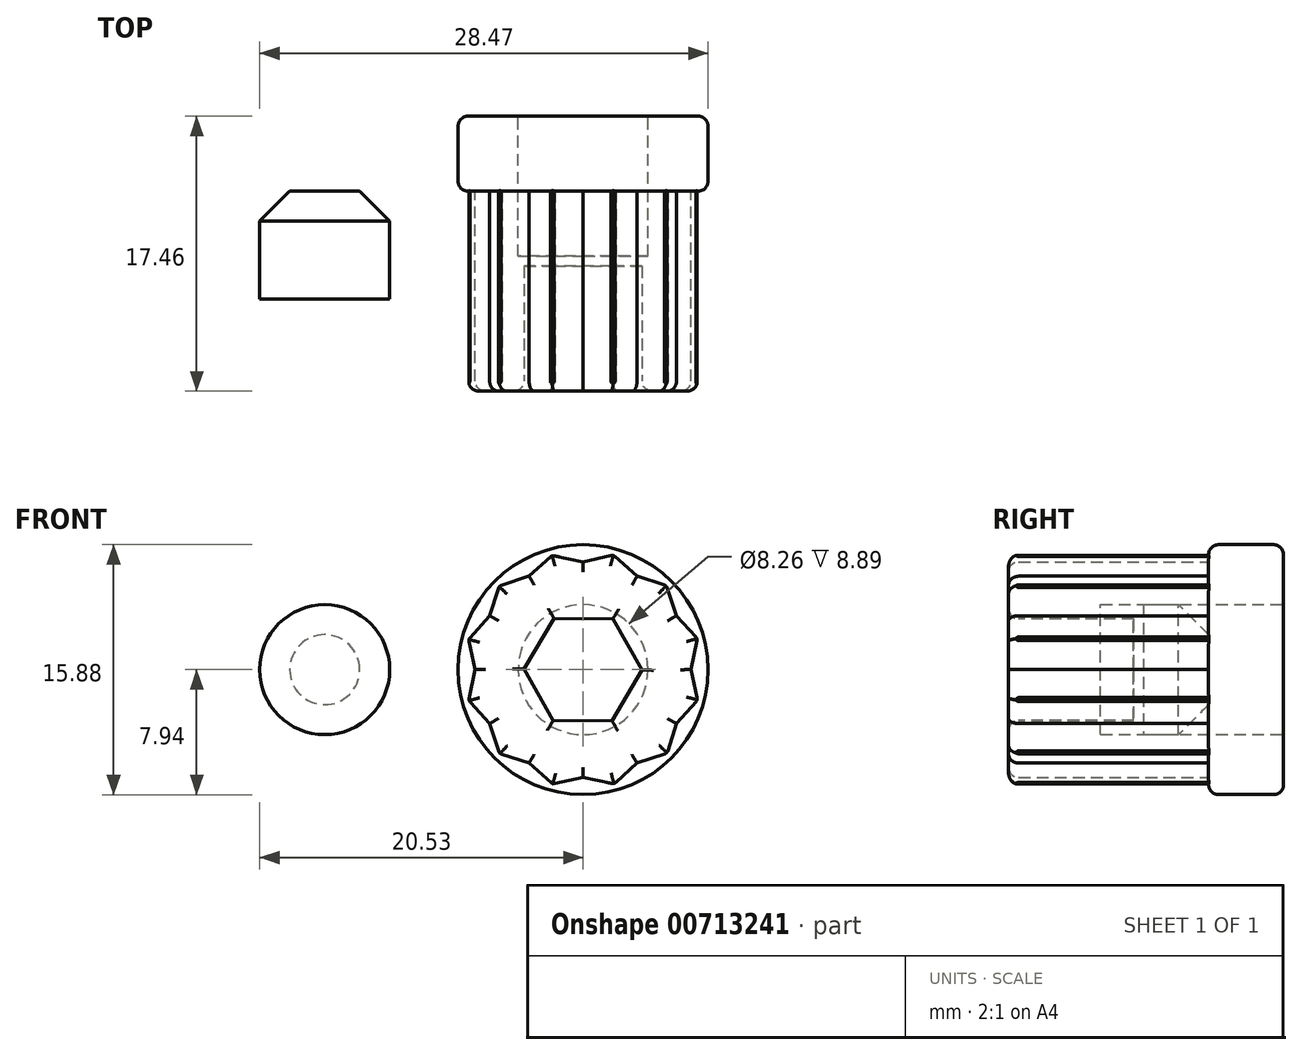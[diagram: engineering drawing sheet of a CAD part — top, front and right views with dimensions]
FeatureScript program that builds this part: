
annotation { "Feature Type Name" : "Feature", "Feature Type Description" : "" }
export const myFeature = defineFeature(function(context is Context, id is Id, definition is map)
    precondition{}
    {
        {
            var Q0;
            Q0=qCreatedBy(makeId("Front.planeOp"),FACE);
            var sketch = newSketch(context, id + "F0", { "sketchPlane" : qUnion([Q0])});
            skCircle(sketch, "E0.cCircle", {"center": v(0, 0) * mm, "radius": 7.24 * mm, "construction": true});
            skLineSegment(sketch, "E0.0", {"start": v(7.24, -1.93) * mm, "end": v(5.3, -5.29) * mm});
            skLineSegment(sketch, "E0.1", {"start": v(5.3, -5.29) * mm, "end": v(1.95, -7.23) * mm});
            skLineSegment(sketch, "E0.2", {"start": v(1.95, -7.23) * mm, "end": v(-1.93, -7.24) * mm});
            skLineSegment(sketch, "E0.3", {"start": v(-1.93, -7.24) * mm, "end": v(-5.29, -5.3) * mm});
            skLineSegment(sketch, "E0.4", {"start": v(-5.29, -5.3) * mm, "end": v(-7.23, -1.95) * mm});
            skLineSegment(sketch, "E0.5", {"start": v(-7.23, -1.95) * mm, "end": v(-7.24, 1.93) * mm});
            skLineSegment(sketch, "E0.6", {"start": v(-7.24, 1.93) * mm, "end": v(-5.3, 5.29) * mm});
            skLineSegment(sketch, "E0.7", {"start": v(-5.3, 5.29) * mm, "end": v(-1.95, 7.23) * mm});
            skLineSegment(sketch, "E0.8", {"start": v(-1.95, 7.23) * mm, "end": v(1.93, 7.24) * mm});
            skLineSegment(sketch, "E0.9", {"start": v(1.93, 7.24) * mm, "end": v(5.29, 5.3) * mm});
            skLineSegment(sketch, "E0.10", {"start": v(5.29, 5.3) * mm, "end": v(7.23, 1.95) * mm});
            skLineSegment(sketch, "E0.11", {"start": v(7.23, 1.95) * mm, "end": v(7.24, -1.93) * mm});
            skPoint(sketch, "E0.0.midPoint", {"position": v(6.27, -3.6) * mm});
            skSolve(sketch);
        }
        {
            var Q0;
            Q0=makeQuery(id+"F0.imprint","IMPRINT",FACE,{"disambiguationData":[TD([[makeQuery(id+"F0.imprint","IMPRINT",EDGE,{"derivedFrom":sQuery(id+"F0.wireOp",EDGE,"E0.0")}),-1.0]])]});
            var sketch = newSketch(context, id + "F1", { "sketchPlane" : qUnion([Q0])});
            skCircle(sketch, "E1", {"center": v(0, 0) * mm, "radius": 6.86 * mm, "construction": true});
            skSolve(sketch);
        }
        {
            var Q0;
            Q0=makeQuery(id+"F1.imprint","IMPRINT",FACE,{"disambiguationData":[TD([[makeQuery(id+"F1.imprint","IMPRINT",EDGE,{"derivedFrom":makeQuery(id+"F0.imprint","IMPRINT",EDGE,{"derivedFrom":sQuery(id+"F0.wireOp",EDGE,"E0.0")})}),-1.0]])]});
            var sketch = newSketch(context, id + "F2", { "sketchPlane" : qUnion([Q0])});
            skLineSegment(sketch, "E2", {"start": v(-1.96, 7.26) * mm, "end": v(0, 6.85) * mm});
            skLineSegment(sketch, "E3", {"start": v(0, 6.85) * mm, "end": v(1.95, 7.28) * mm});
            skLineSegment(sketch, "E4", {"start": v(1.95, 7.28) * mm, "end": v(-1.96, 7.26) * mm});
            skLineSegment(sketch, "E5.1.0", {"start": v(-5.32, 5.3) * mm, "end": v(-3.43, 5.94) * mm});
            skLineSegment(sketch, "E5.1.1", {"start": v(-3.43, 5.94) * mm, "end": v(-1.95, 7.28) * mm});
            skLineSegment(sketch, "E5.1.2", {"start": v(-1.95, 7.28) * mm, "end": v(-5.32, 5.3) * mm});
            skLineSegment(sketch, "E5.2.0", {"start": v(-7.26, 1.93) * mm, "end": v(-5.94, 3.43) * mm});
            skLineSegment(sketch, "E5.2.1", {"start": v(-5.94, 3.43) * mm, "end": v(-5.33, 5.33) * mm});
            skLineSegment(sketch, "E5.2.2", {"start": v(-5.33, 5.33) * mm, "end": v(-7.26, 1.93) * mm});
            skLineSegment(sketch, "E5.3.0", {"start": v(-7.26, -1.96) * mm, "end": v(-6.85, 0) * mm});
            skLineSegment(sketch, "E5.3.1", {"start": v(-6.85, 0) * mm, "end": v(-7.28, 1.95) * mm});
            skLineSegment(sketch, "E5.3.2", {"start": v(-7.28, 1.95) * mm, "end": v(-7.26, -1.96) * mm});
            skLineSegment(sketch, "E5.4.0", {"start": v(-5.3, -5.32) * mm, "end": v(-5.94, -3.43) * mm});
            skLineSegment(sketch, "E5.4.1", {"start": v(-5.94, -3.43) * mm, "end": v(-7.28, -1.95) * mm});
            skLineSegment(sketch, "E5.4.2", {"start": v(-7.28, -1.95) * mm, "end": v(-5.3, -5.32) * mm});
            skLineSegment(sketch, "E5.5.0", {"start": v(-1.93, -7.26) * mm, "end": v(-3.43, -5.94) * mm});
            skLineSegment(sketch, "E5.5.1", {"start": v(-3.43, -5.94) * mm, "end": v(-5.33, -5.33) * mm});
            skLineSegment(sketch, "E5.5.2", {"start": v(-5.33, -5.33) * mm, "end": v(-1.93, -7.26) * mm});
            skLineSegment(sketch, "E5.6.0", {"start": v(1.96, -7.26) * mm, "end": v(0, -6.85) * mm});
            skLineSegment(sketch, "E5.6.1", {"start": v(0, -6.85) * mm, "end": v(-1.95, -7.28) * mm});
            skLineSegment(sketch, "E5.6.2", {"start": v(-1.95, -7.28) * mm, "end": v(1.96, -7.26) * mm});
            skLineSegment(sketch, "E5.7.0", {"start": v(5.32, -5.3) * mm, "end": v(3.43, -5.94) * mm});
            skLineSegment(sketch, "E5.7.1", {"start": v(3.43, -5.94) * mm, "end": v(1.95, -7.28) * mm});
            skLineSegment(sketch, "E5.7.2", {"start": v(1.95, -7.28) * mm, "end": v(5.32, -5.3) * mm});
            skLineSegment(sketch, "E5.8.0", {"start": v(7.26, -1.93) * mm, "end": v(5.94, -3.43) * mm});
            skLineSegment(sketch, "E5.8.1", {"start": v(5.94, -3.43) * mm, "end": v(5.33, -5.33) * mm});
            skLineSegment(sketch, "E5.8.2", {"start": v(5.33, -5.33) * mm, "end": v(7.26, -1.93) * mm});
            skLineSegment(sketch, "E5.9.0", {"start": v(7.26, 1.96) * mm, "end": v(6.85, 0) * mm});
            skLineSegment(sketch, "E5.9.1", {"start": v(6.85, 0) * mm, "end": v(7.28, -1.95) * mm});
            skLineSegment(sketch, "E5.9.2", {"start": v(7.28, -1.95) * mm, "end": v(7.26, 1.96) * mm});
            skLineSegment(sketch, "E5.10.0", {"start": v(5.3, 5.32) * mm, "end": v(5.94, 3.43) * mm});
            skLineSegment(sketch, "E5.10.1", {"start": v(5.94, 3.43) * mm, "end": v(7.28, 1.95) * mm});
            skLineSegment(sketch, "E5.10.2", {"start": v(7.28, 1.95) * mm, "end": v(5.3, 5.32) * mm});
            skLineSegment(sketch, "E5.11.0", {"start": v(1.93, 7.26) * mm, "end": v(3.43, 5.94) * mm});
            skLineSegment(sketch, "E5.11.1", {"start": v(3.43, 5.94) * mm, "end": v(5.33, 5.33) * mm});
            skLineSegment(sketch, "E5.11.2", {"start": v(5.33, 5.33) * mm, "end": v(1.93, 7.26) * mm});
            skPoint(sketch, "E5.center", {"position": v(0, 0) * mm});
            skSolve(sketch);
        }
        {
            var Q0;
            Q0=makeQuery(id+"F1.imprint","IMPRINT",FACE,{"disambiguationData":[TD([[makeQuery(id+"F1.imprint","IMPRINT",EDGE,{"derivedFrom":makeQuery(id+"F0.imprint","IMPRINT",EDGE,{"derivedFrom":sQuery(id+"F0.wireOp",EDGE,"E0.0")})}),-1.0]])]});
            extrude(context, id + "F3", {"entities" : qUnion([Q0]), "depth" : 12.7 * mm, "offsetDistance" : 25.4 * mm});
        }
        {
            var Q0;
            Q0 = qSketchRegion(id + "F2", true);
            extrude(context, id + "F4", {"entities" : qUnion([Q0]), "operationType" : NewBodyOperationType.REMOVE, "endBound" : BoundingType.THROUGH_ALL, "depth" : 25.4 * mm, "offsetDistance" : 25.4 * mm});
        }
        {
            var Q0;
            Q0=makeQuery(id+"F0.imprint","IMPRINT",FACE,{"disambiguationData":[TD([[makeQuery(id+"F0.imprint","IMPRINT",EDGE,{"derivedFrom":sQuery(id+"F0.wireOp",EDGE,"E0.0")}),-1.0]])]});
            var sketch = newSketch(context, id + "F5", { "sketchPlane" : qUnion([Q0])});
            skCircle(sketch, "E6", {"center": v(0, 0) * mm, "radius": 7.94 * mm});
            skSolve(sketch);
        }
        {
            var Q0;
            Q0 = qSketchRegion(id + "F5", true);
            extrude(context, id + "F6", {"entities" : qUnion([Q0]), "operationType" : NewBodyOperationType.ADD, "oppositeDirection" : true, "depth" : 4.76 * mm, "offsetDistance" : 25.4 * mm});
        }
        {
            var Q0;
            Q0=makeQuery(id+"F3.opExtrude","CAP_FACE",FACE,{"disambiguationData":[OSD([sQuery(id+"F0.wireOp",EDGE,"E0.0"),sQuery(id+"F0.wireOp",EDGE,"E0.1"),sQuery(id+"F0.wireOp",EDGE,"E0.2"),sQuery(id+"F0.wireOp",EDGE,"E0.3"),sQuery(id+"F0.wireOp",EDGE,"E0.4"),sQuery(id+"F0.wireOp",EDGE,"E0.5"),sQuery(id+"F0.wireOp",EDGE,"E0.6"),sQuery(id+"F0.wireOp",EDGE,"E0.7"),sQuery(id+"F0.wireOp",EDGE,"E0.8"),sQuery(id+"F0.wireOp",EDGE,"E0.9"),sQuery(id+"F0.wireOp",EDGE,"E0.10"),sQuery(id+"F0.wireOp",EDGE,"E0.11")])],"isStart":false});
            var sketch = newSketch(context, id + "F7", { "sketchPlane" : qUnion([Q0])});
            skCircle(sketch, "E7.cCircle", {"center": v(0, 0) * mm, "radius": 3.24 * mm, "construction": true});
            skLineSegment(sketch, "E7.0", {"start": v(1.9, 3.22) * mm, "end": v(3.74, -0.03) * mm});
            skLineSegment(sketch, "E7.1", {"start": v(3.74, -0.03) * mm, "end": v(1.84, -3.25) * mm});
            skLineSegment(sketch, "E7.2", {"start": v(1.84, -3.25) * mm, "end": v(-1.9, -3.22) * mm});
            skLineSegment(sketch, "E7.3", {"start": v(-1.9, -3.22) * mm, "end": v(-3.74, 0.03) * mm});
            skLineSegment(sketch, "E7.4", {"start": v(-3.74, 0.03) * mm, "end": v(-1.84, 3.25) * mm});
            skLineSegment(sketch, "E7.5", {"start": v(-1.84, 3.25) * mm, "end": v(1.9, 3.22) * mm});
            skPoint(sketch, "E7.0.midPoint", {"position": v(2.82, 1.6) * mm});
            skSolve(sketch);
        }
        {
            var Q0;
            Q0=makeQuery(id+"F7.imprint","IMPRINT",FACE,{"disambiguationData":[TD([[makeQuery(id+"F7.imprint","IMPRINT",EDGE,{"derivedFrom":sQuery(id+"F7.wireOp",EDGE,"E7.0")}),-1.0]])]});
            extrude(context, id + "F8", {"entities" : qUnion([Q0]), "operationType" : NewBodyOperationType.REMOVE, "oppositeDirection" : true, "depth" : 7.94 * mm, "offsetDistance" : 25.4 * mm});
        }
        {
            var Q0;
            Q0=makeQuery(id+"F3.opExtrude","CAP_FACE",FACE,{"disambiguationData":[OSD([sQuery(id+"F0.wireOp",EDGE,"E0.0"),sQuery(id+"F0.wireOp",EDGE,"E0.1"),sQuery(id+"F0.wireOp",EDGE,"E0.2"),sQuery(id+"F0.wireOp",EDGE,"E0.3"),sQuery(id+"F0.wireOp",EDGE,"E0.4"),sQuery(id+"F0.wireOp",EDGE,"E0.5"),sQuery(id+"F0.wireOp",EDGE,"E0.6"),sQuery(id+"F0.wireOp",EDGE,"E0.7"),sQuery(id+"F0.wireOp",EDGE,"E0.8"),sQuery(id+"F0.wireOp",EDGE,"E0.9"),sQuery(id+"F0.wireOp",EDGE,"E0.10"),sQuery(id+"F0.wireOp",EDGE,"E0.11")])],"isStart":false});
            var Q1;
            Q1=makeQuery(id+"F6.opExtrude","CAP_EDGE",EDGE,{"disambiguationData":[OSD([sQuery(id+"F5.wireOp",EDGE,"E6")])],"isStart":true});
            var Q2;
            Q2=makeQuery(id+"F6.opExtrude","CAP_EDGE",EDGE,{"disambiguationData":[OSD([sQuery(id+"F5.wireOp",EDGE,"E6")])],"isStart":false});
            fillet(context, id + "F9", {"entities" : qUnion([Q0, Q1, Q2]), "radius" : 0.64 * mm, "tangentPropagation" : true, "allowEdgeOverflow" : false});
        }
        {
            var Q0;
            Q0=makeQuery(id+"F6.opExtrude","CAP_FACE",FACE,{"disambiguationData":[OSD([sQuery(id+"F5.wireOp",EDGE,"E6")])],"isStart":false});
            var sketch = newSketch(context, id + "F10", { "sketchPlane" : qUnion([Q0])});
            skCircle(sketch, "E8", {"center": v(0, 0) * mm, "radius": 4.13 * mm});
            skSolve(sketch);
        }
        {
            var Q0;
            Q0=makeQuery(id+"F10.imprint","IMPRINT",FACE,{"disambiguationData":[TD([[makeQuery(id+"F10.imprint","IMPRINT",EDGE,{"derivedFrom":sQuery(id+"F10.wireOp",EDGE,"E8")}),1.0]])]});
            extrude(context, id + "F11", {"entities" : qUnion([Q0]), "operationType" : NewBodyOperationType.REMOVE, "oppositeDirection" : true, "depth" : 8.9 * mm, "offsetDistance" : 25.4 * mm});
        }
        {
            var Q0;
            Q0=qCreatedBy(makeId("Front.planeOp"),FACE);
            var sketch = newSketch(context, id + "F12", { "sketchPlane" : qUnion([Q0])});
            skCircle(sketch, "E9", {"center": v(-16.4, 0) * mm, "radius": 4.13 * mm});
            skSolve(sketch);
        }
        {
            var Q0;
            Q0 = qSketchRegion(id + "F12", true);
            extrude(context, id + "F13", {"entities" : qUnion([Q0]), "depth" : 6.86 * mm, "offsetDistance" : 25.4 * mm});
        }
        {
            var Q0;
            Q0=makeQuery(id+"F13.opExtrude","CAP_EDGE",EDGE,{"disambiguationData":[OSD([sQuery(id+"F12.wireOp",EDGE,"E9")])],"isStart":true});
            chamfer(context, id + "F14", {"entities" : qUnion([Q0]), "width" : 1.9 * mm, "tangentPropagation" : true});
        }
    });
